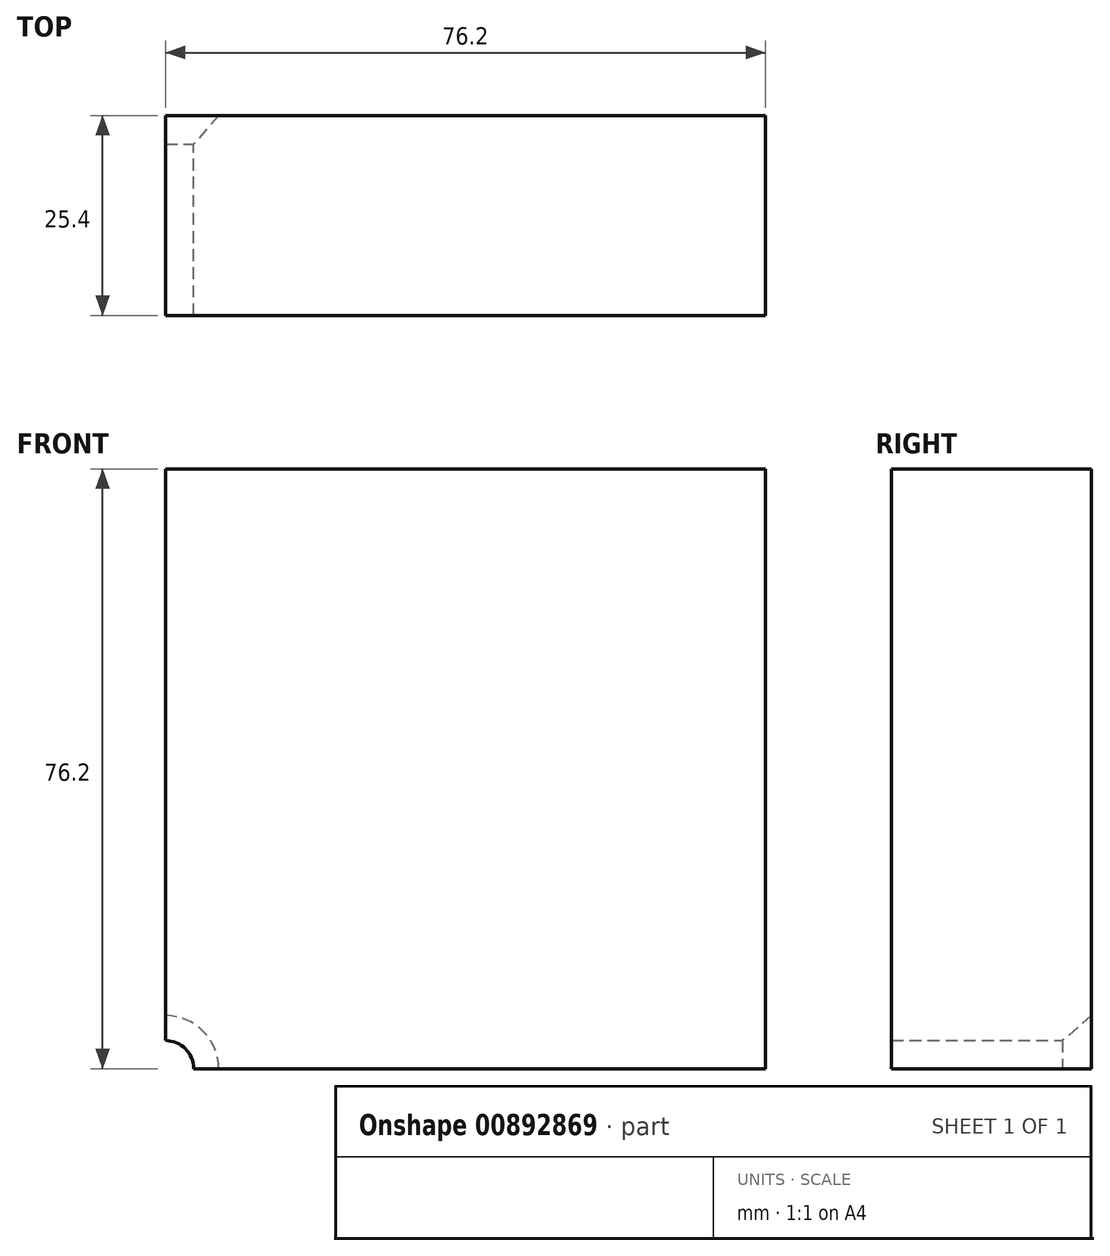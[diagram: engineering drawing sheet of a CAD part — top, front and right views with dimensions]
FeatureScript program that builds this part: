
annotation { "Feature Type Name" : "Feature", "Feature Type Description" : "" }
export const myFeature = defineFeature(function(context is Context, id is Id, definition is map)
    precondition{}
    {
        {
            var Q0;
            Q0=qCreatedBy(makeId("Front.planeOp"),FACE);
            var sketch = newSketch(context, id + "F0", { "sketchPlane" : qUnion([Q0])});
            skLineSegment(sketch, "E0.bottom", {"start": v(38.1, 38.1) * mm, "end": v(-38.1, 38.1) * mm});
            skLineSegment(sketch, "E0.top", {"start": v(38.1, -38.1) * mm, "end": v(-38.1, -38.1) * mm});
            skLineSegment(sketch, "E0.left", {"start": v(38.1, 38.1) * mm, "end": v(38.1, -38.1) * mm});
            skLineSegment(sketch, "E0.right", {"start": v(-38.1, 38.1) * mm, "end": v(-38.1, -38.1) * mm});
            skPoint(sketch, "E0.middle", {"position": v(0, 0) * mm});
            skSolve(sketch);
        }
        {
            var Q0;
            Q0 = qSketchRegion(id + "F0", true);
            extrude(context, id + "F1", {"entities" : qUnion([Q0]), "depth" : 25.4 * mm, "offsetDistance" : 25.4 * mm});
        }
        {
            var Q0;
            Q0=sQuery(id+"F0.wireOp",VERTEX,"E0.top.end");
            var Q1;
            Q1=makeQuery(id+"F1.opExtrude","SWEPT_BODY",BODY,{"disambiguationData":[OSD([sQuery(id+"F0.wireOp",EDGE,"E0.bottom"),sQuery(id+"F0.wireOp",EDGE,"E0.top"),sQuery(id+"F0.wireOp",EDGE,"E0.left"),sQuery(id+"F0.wireOp",EDGE,"E0.right")])]});
            hole(context, id + "F2", {"style" : HoleStyle.C_SINK, "endStyle" : HoleEndStyle.THROUGH, "oppositeDirection" : true, "holeDiameter" : 7.14 * mm, "cSinkDiameter" : 13.5 * mm, "cSinkAngle" : 82 * degree, "majorDiameter" : 6.35 * mm, "isTappedThrough" : true, "tappedDepth" : 12.7 * mm, "tapClearance" : 3, "locations" : qUnion([Q0]), "scope" : qUnion([Q1])});
        }
    });
